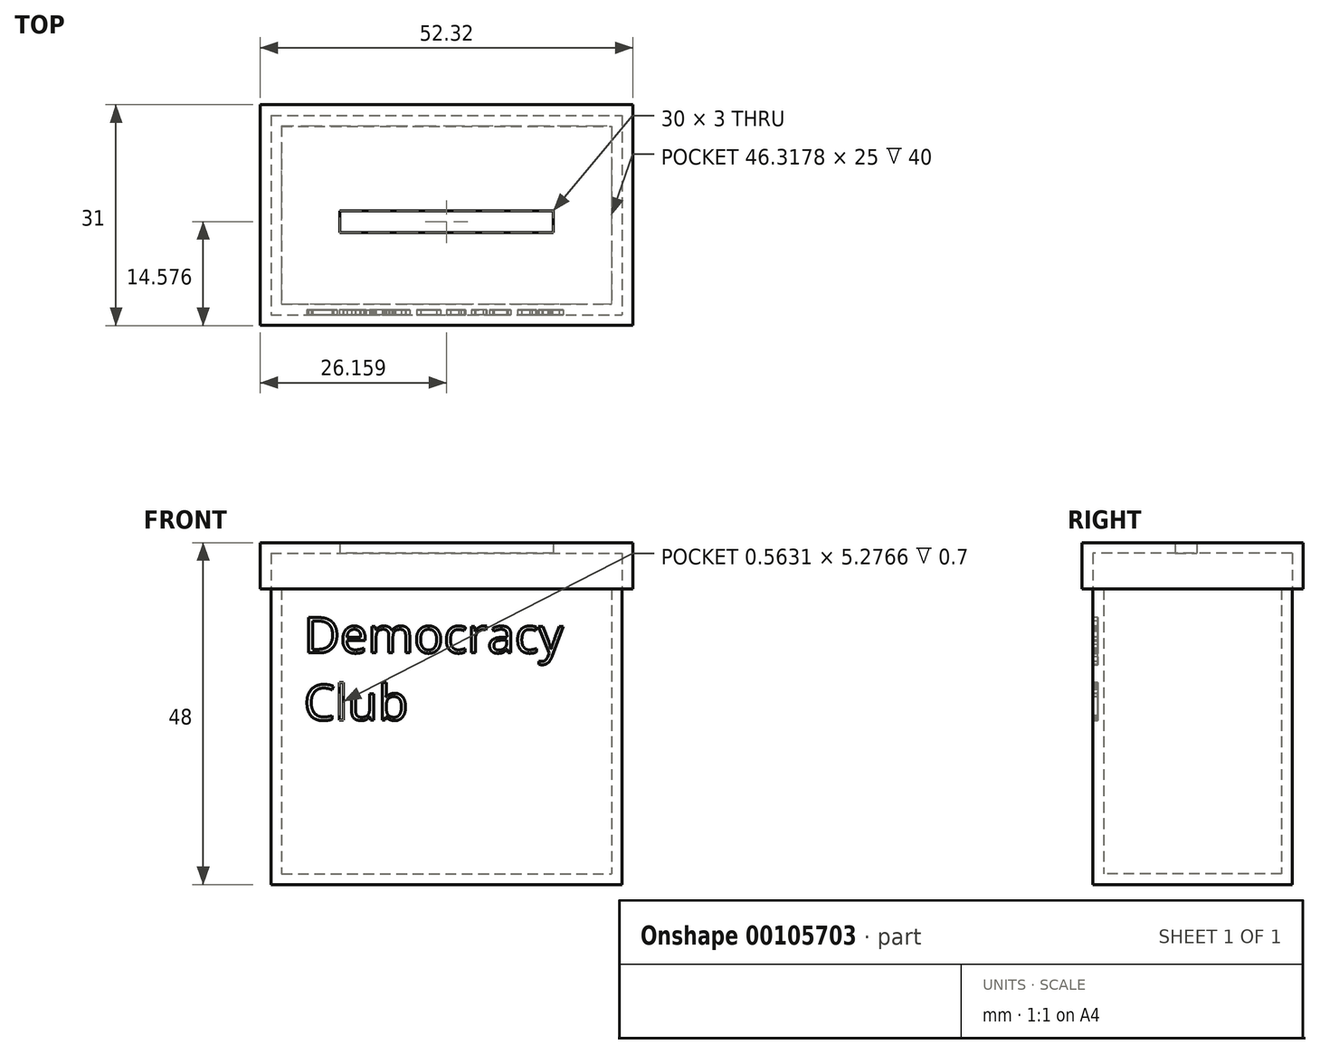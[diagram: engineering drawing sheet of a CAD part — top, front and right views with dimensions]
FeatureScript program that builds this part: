
annotation { "Feature Type Name" : "Feature", "Feature Type Description" : "" }
export const myFeature = defineFeature(function(context is Context, id is Id, definition is map)
    precondition{}
    {
        {
            var Q0;
            Q0=qCreatedBy(makeId("Top.planeOp"),FACE);
            var sketch = newSketch(context, id + "F0", { "sketchPlane" : qUnion([Q0])});
            skLineSegment(sketch, "E0.bottom", {"start": v(-39.2, -8.87) * mm, "end": v(7.12, -8.87) * mm});
            skLineSegment(sketch, "E0.top", {"start": v(-39.2, -33.87) * mm, "end": v(7.12, -33.87) * mm});
            skLineSegment(sketch, "E0.left", {"start": v(-39.2, -8.87) * mm, "end": v(-39.2, -33.87) * mm});
            skLineSegment(sketch, "E0.right", {"start": v(7.12, -8.87) * mm, "end": v(7.12, -33.87) * mm});
            skLineSegment(sketch, "E1.bottom", {"start": v(-31.04, -20.8) * mm, "end": v(-1.04, -20.8) * mm});
            skLineSegment(sketch, "E1.top", {"start": v(-31.04, -23.8) * mm, "end": v(-1.04, -23.8) * mm});
            skLineSegment(sketch, "E1.left", {"start": v(-31.04, -20.8) * mm, "end": v(-31.04, -23.8) * mm});
            skLineSegment(sketch, "E1.right", {"start": v(-1.04, -20.8) * mm, "end": v(-1.04, -23.8) * mm});
            skLineSegment(sketch, "E2", {"start": v(-16.04, -8.87) * mm, "end": v(-16.04, -20.8) * mm});
            skSolve(sketch);
        }
        {
            var Q0;
            Q0=makeQuery(id+"F0.imprint","IMPRINT",FACE,{"disambiguationData":[TD([[makeQuery(id+"F0.imprint","IMPRINT",EDGE,{"derivedFrom":sQuery(id+"F0.wireOp",EDGE,"E0.top")}),1.0]])]});
            var Q1;
            Q1=makeQuery(id+"F0.imprint","IMPRINT",FACE,{"disambiguationData":[TD([[makeQuery(id+"F0.imprint","IMPRINT",EDGE,{"derivedFrom":sQuery(id+"F0.wireOp",EDGE,"E1.top")}),1.0]])]});
            extrude(context, id + "F1", {"entities" : qUnion([Q0, Q1]), "depth" : 40 * mm});
        }
        {
            var Q0;
            Q0=makeQuery(id+"F1.opExtrude","CAP_FACE",FACE,{"disambiguationData":[OSD([sQuery(id+"F0.wireOp",EDGE,"E0.bottom"),sQuery(id+"F0.wireOp",EDGE,"E0.top"),sQuery(id+"F0.wireOp",EDGE,"E0.left"),sQuery(id+"F0.wireOp",EDGE,"E0.right")])],"isStart":false});
            shell(context, id + "F2", {"entities" : qUnion([Q0]), "thickness" : 1.5 * mm, "oppositeDirection" : true});
        }
        {
            var Q0;
            Q0=makeQuery(id+"F1.opExtrude","SWEPT_FACE",FACE,{"disambiguationData":[OSD([sQuery(id+"F0.wireOp",EDGE,"E0.top")])]});
            var sketch = newSketch(context, id + "F3", { "sketchPlane" : qUnion([Q0])});
            skText(sketch, "E3", { "text": "Democracy\nClub", "fontName": "OpenSans-Regular.ttf"});
            const initialGuessF3  = {"E3": [-0.03607, 0.03103, 1, 0, 0.005]};
            skSetInitialGuess(sketch, initialGuessF3);
            skSolve(sketch);
        }
        {
            var Q0;
            Q0 = qSketchRegion(id + "F3", true);
            extrude(context, id + "F4", {"entities" : qUnion([Q0]), "operationType" : NewBodyOperationType.REMOVE, "oppositeDirection" : true, "depth" : 0.7 * mm});
        }
        {
            var Q0;
            Q0=makeQuery(id+"F1.opExtrude","CAP_FACE",FACE,{"disambiguationData":[OSD([sQuery(id+"F0.wireOp",EDGE,"E0.bottom"),sQuery(id+"F0.wireOp",EDGE,"E0.top"),sQuery(id+"F0.wireOp",EDGE,"E0.left"),sQuery(id+"F0.wireOp",EDGE,"E0.right")])],"isStart":false});
            var sketch = newSketch(context, id + "F5", { "sketchPlane" : qUnion([Q0])});
            skLineSegment(sketch, "E4.0", {"start": v(-40.7, -7.37) * mm, "end": v(8.62, -7.37) * mm});
            skLineSegment(sketch, "E5.0", {"start": v(-40.7, -7.37) * mm, "end": v(-40.7, -35.37) * mm});
            skLineSegment(sketch, "E6.0", {"start": v(-40.7, -35.37) * mm, "end": v(8.62, -35.37) * mm});
            skLineSegment(sketch, "E7.0", {"start": v(8.62, -7.37) * mm, "end": v(8.62, -35.37) * mm});
            skSolve(sketch);
        }
        {
            var Q0;
            Q0 = qSketchRegion(id + "F5", true);
            var Q1;
            {var subQ0=sQuery(id+"F0.wireOp",EDGE,"E0.bottom");Q1=makeQuery(id+"F5.imprint","IMPRINT",FACE,{"disambiguationData":[TD([[makeQuery(id+"F5.imprint","IMPRINT",EDGE,{"derivedFrom":makeQuery(id+"F2.opShell","OFFSET_EDGE",EDGE,{"disambiguationData":[OSD([subQ0]),TDD([makeQuery(id+"F1.opExtrude","CAP_EDGE",EDGE,{"disambiguationData":[OSD([subQ0])],"isStart":false})])]})}),-1.0]])]});}
            extrude(context, id + "F6", {"entities" : qUnion([Q0, Q1]), "depth" : 5 * mm});
        }
        {
            var Q0;
            Q0=makeQuery(id+"F6.opExtrude","CAP_FACE",FACE,{"disambiguationData":[OSD([sQuery(id+"F5.wireOp",EDGE,"E4.0"),sQuery(id+"F5.wireOp",EDGE,"E5.0"),sQuery(id+"F5.wireOp",EDGE,"E6.0"),sQuery(id+"F5.wireOp",EDGE,"E7.0")])],"isStart":true});
            shell(context, id + "F7", {"entities" : qUnion([Q0]), "thickness" : 1.5 * mm, "oppositeDirection" : true});
        }
        {
            var Q0;
            Q0=makeQuery(id+"F0.imprint","IMPRINT",FACE,{"disambiguationData":[TD([[makeQuery(id+"F0.imprint","IMPRINT",EDGE,{"derivedFrom":sQuery(id+"F0.wireOp",EDGE,"E1.top")}),1.0]])]});
            extrude(context, id + "F8", {"entities" : qUnion([Q0]), "operationType" : NewBodyOperationType.REMOVE, "depth" : 74.24 * mm});
        }
    });
